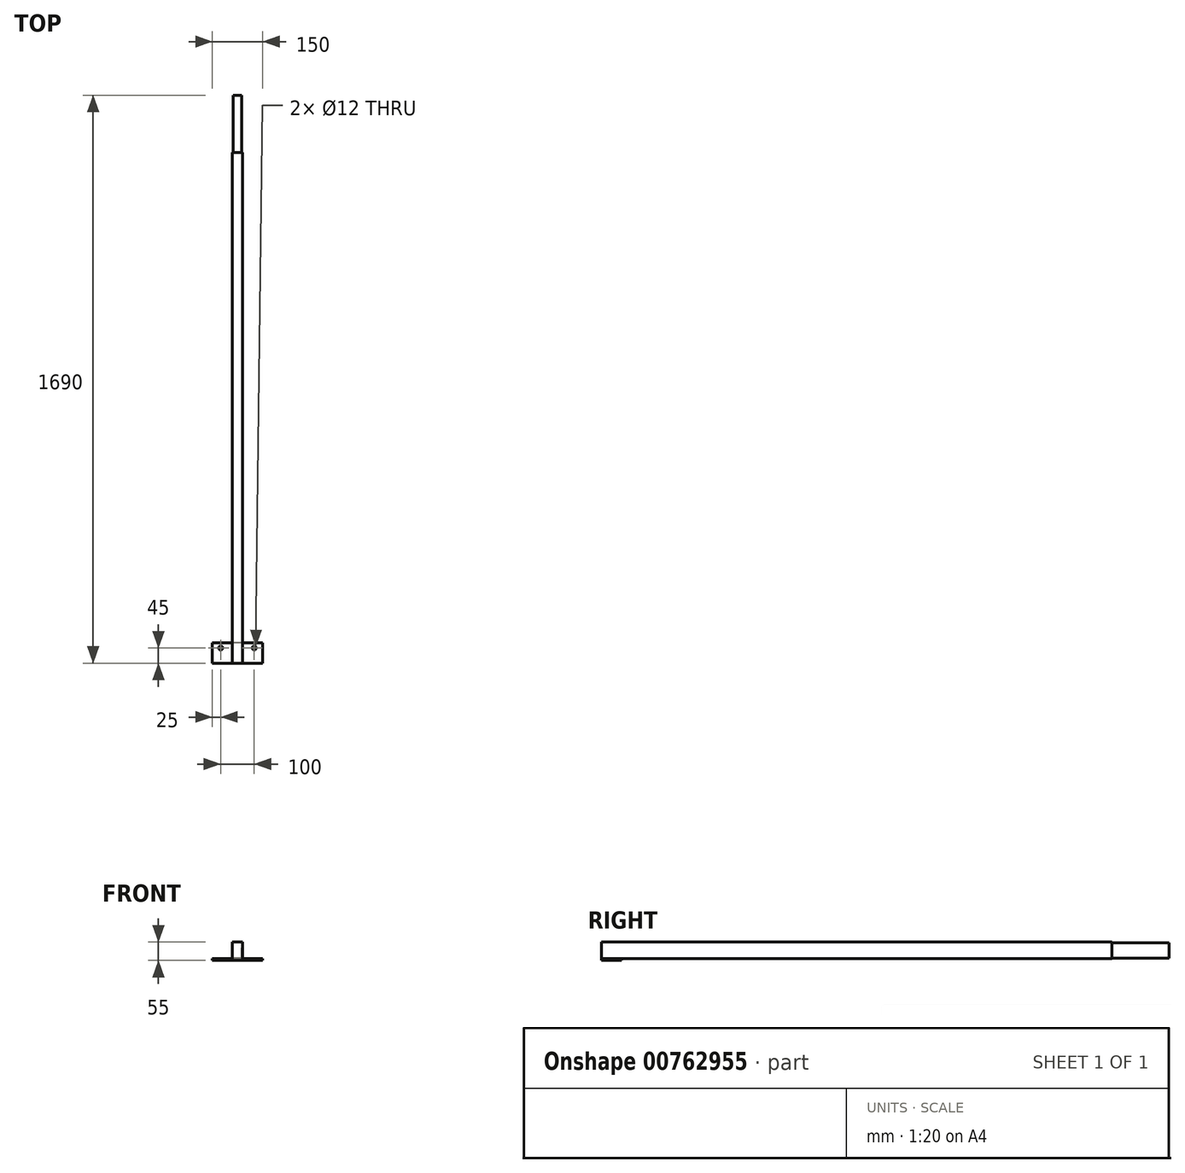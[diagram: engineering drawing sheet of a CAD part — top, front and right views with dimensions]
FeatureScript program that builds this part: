
annotation { "Feature Type Name" : "Feature", "Feature Type Description" : "" }
export const myFeature = defineFeature(function(context is Context, id is Id, definition is map)
    precondition{}
    {
        {
            var Q0;
            Q0=qCreatedBy(makeId("Front.planeOp"),FACE);
            var sketch = newSketch(context, id + "F0", { "sketchPlane" : qUnion([Q0])});
            skLineSegment(sketch, "E0.bottom", {"start": v(13, -23) * mm, "end": v(-13, -23) * mm});
            skLineSegment(sketch, "E0.top", {"start": v(13, 23) * mm, "end": v(-13, 23) * mm});
            skLineSegment(sketch, "E0.left", {"start": v(13, -23) * mm, "end": v(13, 23) * mm});
            skLineSegment(sketch, "E0.right", {"start": v(-13, -23) * mm, "end": v(-13, 23) * mm});
            skPoint(sketch, "E0.middle", {"position": v(0, 0) * mm});
            skSolve(sketch);
        }
        {
            var Q0;
            Q0=qSketchRegion(id+"F0",true);
            extrude(context, id + "F1", {"entities" : qUnion([Q0]), "depth" : 170 * mm, "offsetDistance" : 25 * mm});
        }
        {
            var Q0;
            Q0=makeQuery(id+"F1.opExtrude","CAP_FACE",FACE,{"disambiguationData":[OSD([sQuery(id+"F0.wireOp",EDGE,"E0.bottom"),sQuery(id+"F0.wireOp",EDGE,"E0.top"),sQuery(id+"F0.wireOp",EDGE,"E0.left"),sQuery(id+"F0.wireOp",EDGE,"E0.right")])],"isStart":false});
            var sketch = newSketch(context, id + "F2", { "sketchPlane" : qUnion([Q0])});
            skLineSegment(sketch, "E1.bottom", {"start": v(15, -25) * mm, "end": v(-15, -25) * mm});
            skLineSegment(sketch, "E1.top", {"start": v(15, 25) * mm, "end": v(-15, 25) * mm});
            skLineSegment(sketch, "E1.left", {"start": v(15, -25) * mm, "end": v(15, 25) * mm});
            skLineSegment(sketch, "E1.right", {"start": v(-15, -25) * mm, "end": v(-15, 25) * mm});
            skPoint(sketch, "E1.middle", {"position": v(0, 0) * mm});
            skSolve(sketch);
        }
        {
            var Q0;
            Q0=qSketchRegion(id+"F2",true);
            extrude(context, id + "F3", {"entities" : qUnion([Q0]), "operationType" : NewBodyOperationType.ADD, "depth" : 1520 * mm, "offsetDistance" : 25 * mm});
        }
        {
            var Q0;
            Q0=makeQuery(id+"F3.opExtrude","SWEPT_FACE",FACE,{"disambiguationData":[OSD([sQuery(id+"F2.wireOp",EDGE,"E1.bottom")])]});
            var sketch = newSketch(context, id + "F4", { "sketchPlane" : qUnion([Q0])});
            skLineSegment(sketch, "E2.bottom", {"start": v(-15, 1690) * mm, "end": v(15, 1690) * mm});
            skLineSegment(sketch, "E2.top", {"start": v(-15, 1630) * mm, "end": v(15, 1630) * mm});
            skLineSegment(sketch, "E2.left", {"start": v(-15, 1690) * mm, "end": v(-15, 1630) * mm});
            skLineSegment(sketch, "E2.right", {"start": v(15, 1690) * mm, "end": v(15, 1630) * mm});
            skLineSegment(sketch, "E3.bottom", {"start": v(15, 1690) * mm, "end": v(75, 1690) * mm});
            skLineSegment(sketch, "E3.top", {"start": v(15, 1630) * mm, "end": v(75, 1630) * mm});
            skLineSegment(sketch, "E3.right", {"start": v(75, 1690) * mm, "end": v(75, 1630) * mm});
            skLineSegment(sketch, "E4", {"start": v(15, 1645) * mm, "end": v(50, 1645) * mm});
            skCircle(sketch, "E5", {"center": v(50, 1645) * mm, "radius": 6 * mm});
            skLineSegment(sketch, "E6", {"start": v(-15, 1690) * mm, "end": v(15, 1690) * mm, "construction": true});
            skLineSegment(sketch, "E7", {"start": v(0, 1690) * mm, "end": v(0, 1630) * mm, "construction": true});
            skLineSegment(sketch, "E8.MirrorCS", {"start": v(-15, 1690) * mm, "end": v(-75, 1690) * mm});
            skCircle(sketch, "E9.MirrorC", {"center": v(-50, 1645) * mm, "radius": 6 * mm});
            skLineSegment(sketch, "E10.MirrorCS", {"start": v(-15, 1630) * mm, "end": v(-75, 1630) * mm});
            skLineSegment(sketch, "E11.MirrorCS", {"start": v(-75, 1690) * mm, "end": v(-75, 1630) * mm});
            skSolve(sketch);
        }
        {
            var Q0;
            Q0=qSketchRegion(id+"F4",true);
            extrude(context, id + "F5", {"entities" : qUnion([Q0]), "operationType" : NewBodyOperationType.ADD, "depth" : 5 * mm, "offsetDistance" : 25 * mm});
        }
    });
